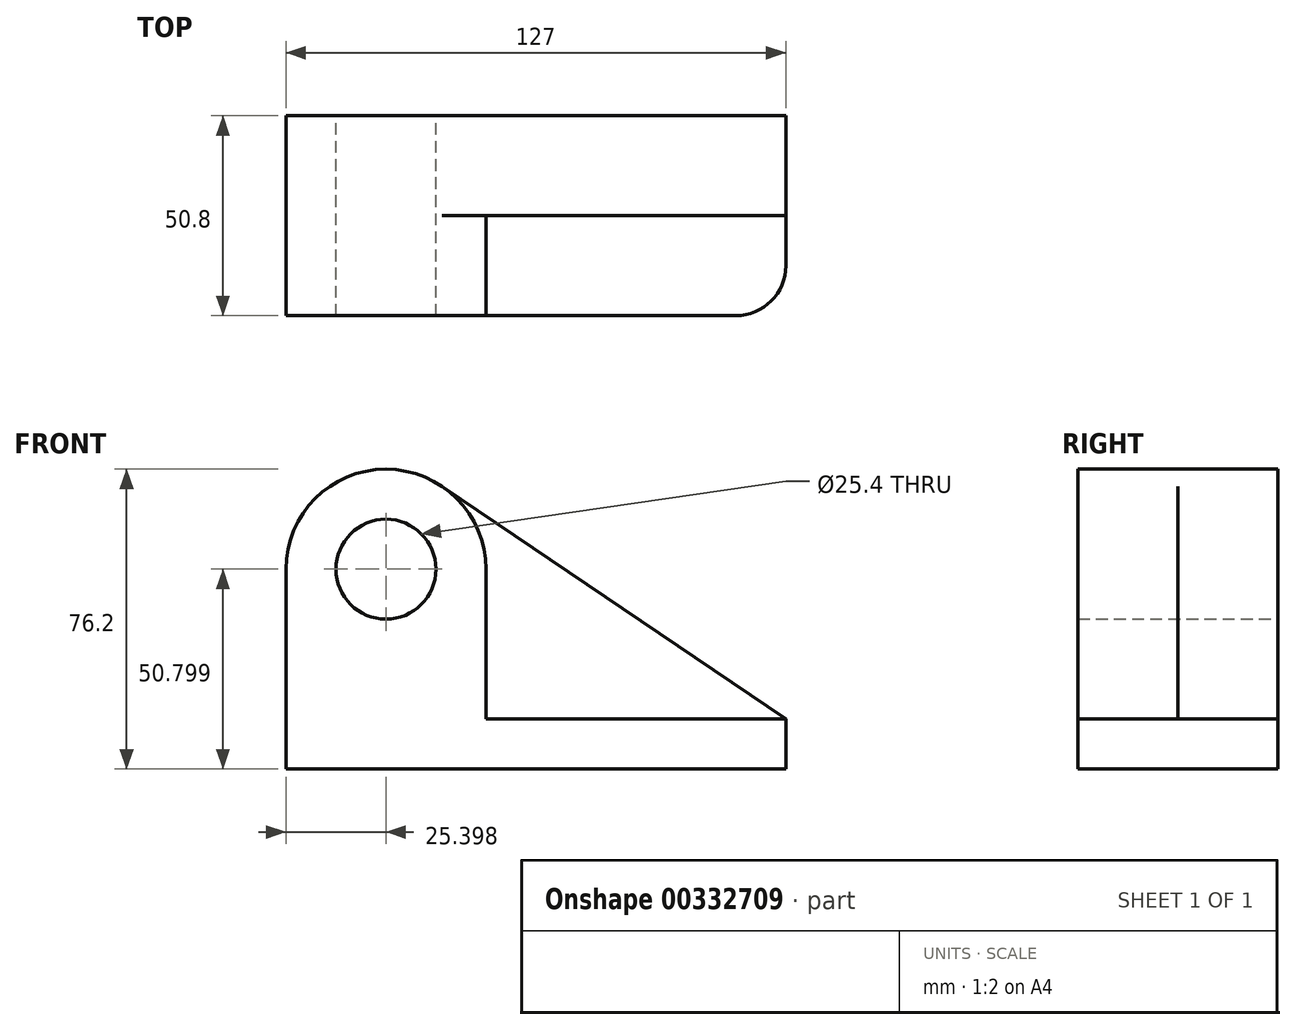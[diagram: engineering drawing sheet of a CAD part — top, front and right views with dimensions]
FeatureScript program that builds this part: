
annotation { "Feature Type Name" : "Feature", "Feature Type Description" : "" }
export const myFeature = defineFeature(function(context is Context, id is Id, definition is map)
    precondition{}
    {
        {
            var Q0;
            Q0=qCreatedBy(makeId("Front.planeOp"),FACE);
            var sketch = newSketch(context, id + "F0", { "sketchPlane" : qUnion([Q0])});
            skCircle(sketch, "E0", {"center": v(-51, 18.34) * mm, "radius": 12.7 * mm});
            skArc(sketch, "E1", {"start": v(-36.75, 39.37) * mm, "mid": v(-62.9, 40.78) * mm, "end": v(-76.4, 18.34) * mm});
            skLineSegment(sketch, "E2", {"start": v(-76.4, 18.34) * mm, "end": v(-76.4, -32.46) * mm});
            skLineSegment(sketch, "E3", {"start": v(-76.4, -32.46) * mm, "end": v(50.6, -32.46) * mm});
            skLineSegment(sketch, "E4", {"start": v(50.6, -32.46) * mm, "end": v(50.6, -19.76) * mm});
            skLineSegment(sketch, "E5", {"start": v(50.6, -19.76) * mm, "end": v(-36.75, 39.37) * mm});
            skSolve(sketch);
        }
        {
            var Q0;
            Q0=makeQuery(id+"F0.imprint","IMPRINT",FACE,{"disambiguationData":[TD([[makeQuery(id+"F0.imprint","IMPRINT",EDGE,{"derivedFrom":sQuery(id+"F0.wireOp",EDGE,"E0")}),-1.0]])]});
            extrude(context, id + "F1", {"entities" : qUnion([Q0]), "depth" : 25.4 * mm});
        }
        {
            var Q0;
            Q0=makeQuery(id+"F1.opExtrude","CAP_FACE",FACE,{"disambiguationData":[OSD([sQuery(id+"F0.wireOp",EDGE,"E0"),sQuery(id+"F0.wireOp",EDGE,"E1"),sQuery(id+"F0.wireOp",EDGE,"E2"),sQuery(id+"F0.wireOp",EDGE,"E3"),sQuery(id+"F0.wireOp",EDGE,"E4"),sQuery(id+"F0.wireOp",EDGE,"E5")])],"isStart":false});
            var sketch = newSketch(context, id + "F2", { "sketchPlane" : qUnion([Q0])});
            skCircle(sketch, "E6", {"center": v(-51, 18.34) * mm, "radius": 12.7 * mm});
            skArc(sketch, "E7", {"start": v(-25.6, 18.34) * mm, "mid": v(-51, 43.74) * mm, "end": v(-76.4, 18.34) * mm});
            skLineSegment(sketch, "E8.bottom", {"start": v(50.6, -19.76) * mm, "end": v(-25.6, -19.76) * mm});
            skLineSegment(sketch, "E8.top", {"start": v(50.6, -32.46) * mm, "end": v(-76.4, -32.46) * mm});
            skLineSegment(sketch, "E8.left", {"start": v(50.6, -19.76) * mm, "end": v(50.6, -32.46) * mm});
            skLineSegment(sketch, "E8.right", {"start": v(-76.4, -19.76) * mm, "end": v(-76.4, -32.46) * mm});
            skLineSegment(sketch, "E9", {"start": v(-76.4, 18.34) * mm, "end": v(-76.4, -19.76) * mm});
            skLineSegment(sketch, "E10", {"start": v(-25.6, 18.34) * mm, "end": v(-25.6, -19.76) * mm});
            skSolve(sketch);
        }
        {
            var Q0;
            Q0 = qSketchRegion(id + "F2", true);
            extrude(context, id + "F3", {"entities" : qUnion([Q0]), "operationType" : NewBodyOperationType.ADD, "depth" : 25.4 * mm});
        }
        {
            var Q0;
            Q0=makeQuery(id+"F3.opExtrude","CAP_EDGE",EDGE,{"disambiguationData":[OSD([sQuery(id+"F2.wireOp",EDGE,"E8.left")])],"isStart":false});
            fillet(context, id + "F4", {"entities" : qUnion([Q0]), "radius" : 12.7 * mm, "tangentPropagation" : true, "allowEdgeOverflow" : false});
        }
    });
